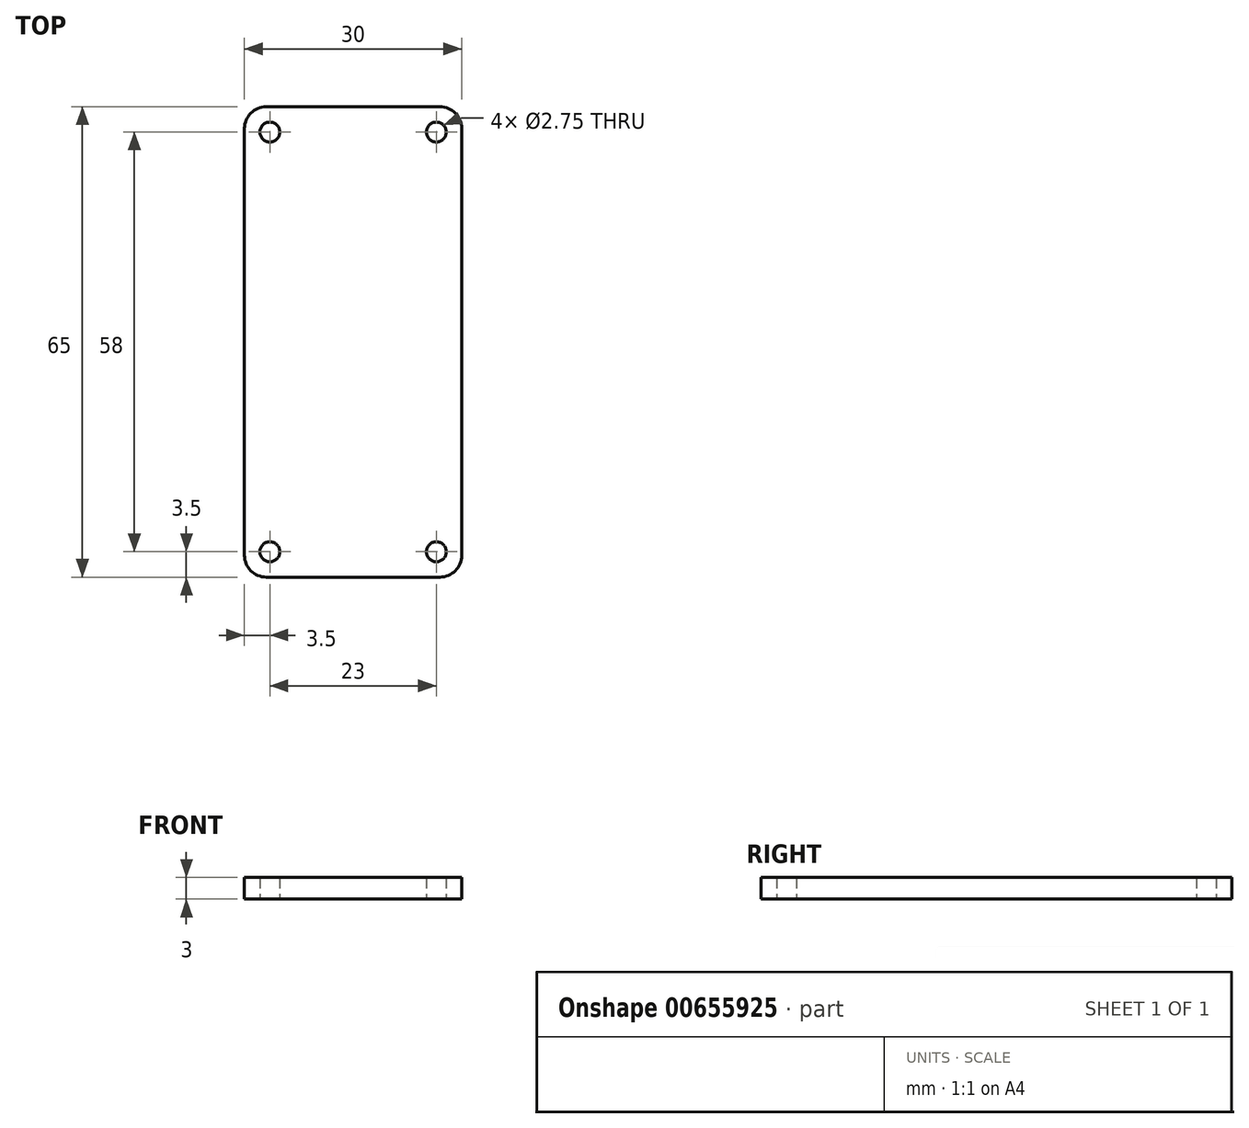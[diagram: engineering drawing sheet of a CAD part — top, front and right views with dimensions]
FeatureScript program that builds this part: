
annotation { "Feature Type Name" : "Feature", "Feature Type Description" : "" }
export const myFeature = defineFeature(function(context is Context, id is Id, definition is map)
    precondition{}
    {
        {
            var Q0;
            Q0=qCreatedBy(makeId("Top.planeOp"),FACE);
            var sketch = newSketch(context, id + "F0", { "sketchPlane" : qUnion([Q0])});
            skLineSegment(sketch, "E0.bottom", {"start": v(12, -32.5) * mm, "end": v(-12, -32.5) * mm});
            skLineSegment(sketch, "E0.top", {"start": v(12, 32.5) * mm, "end": v(-12, 32.5) * mm});
            skLineSegment(sketch, "E0.left", {"start": v(15, -29.5) * mm, "end": v(15, 29.5) * mm});
            skLineSegment(sketch, "E0.right", {"start": v(-15, -29.5) * mm, "end": v(-15, 29.5) * mm});
            skPoint(sketch, "E0.middle", {"position": v(0, 0) * mm});
            skPoint(sketch, "E1.visualSharp", {"position": v(-15, 32.5) * mm});
            skArc(sketch, "E1.filletArc", {"start": v(-12, 32.5) * mm, "mid": v(-14.12, 31.62) * mm, "end": v(-15, 29.5) * mm});
            skPoint(sketch, "E2.visualSharp", {"position": v(15, 32.5) * mm});
            skArc(sketch, "E2.filletArc", {"start": v(15, 29.5) * mm, "mid": v(14.12, 31.62) * mm, "end": v(12, 32.5) * mm});
            skPoint(sketch, "E3.visualSharp", {"position": v(15, -32.5) * mm});
            skArc(sketch, "E3.filletArc", {"start": v(12, -32.5) * mm, "mid": v(14.12, -31.62) * mm, "end": v(15, -29.5) * mm});
            skPoint(sketch, "E4.visualSharp", {"position": v(-15, -32.5) * mm});
            skArc(sketch, "E4.filletArc", {"start": v(-15, -29.5) * mm, "mid": v(-14.12, -31.62) * mm, "end": v(-12, -32.5) * mm});
            skCircle(sketch, "E5", {"center": v(-11.5, 29) * mm, "radius": 1.38 * mm});
            skCircle(sketch, "E6.MirrorC", {"center": v(11.5, 29) * mm, "radius": 1.38 * mm});
            skCircle(sketch, "E7.MirrorC", {"center": v(11.5, -29) * mm, "radius": 1.38 * mm});
            skCircle(sketch, "E8.MirrorC", {"center": v(-11.5, -29) * mm, "radius": 1.38 * mm});
            skSolve(sketch);
        }
        {
            var Q0;
            Q0=makeQuery(id+"F0.imprint","IMPRINT",FACE,{"disambiguationData":[TD([[makeQuery(id+"F0.imprint","IMPRINT",EDGE,{"derivedFrom":sQuery(id+"F0.wireOp",EDGE,"E0.bottom")}),-1.0]])]});
            extrude(context, id + "F1", {"entities" : qUnion([Q0]), "depth" : 3 * mm, "offsetDistance" : 25 * mm});
        }
    });
